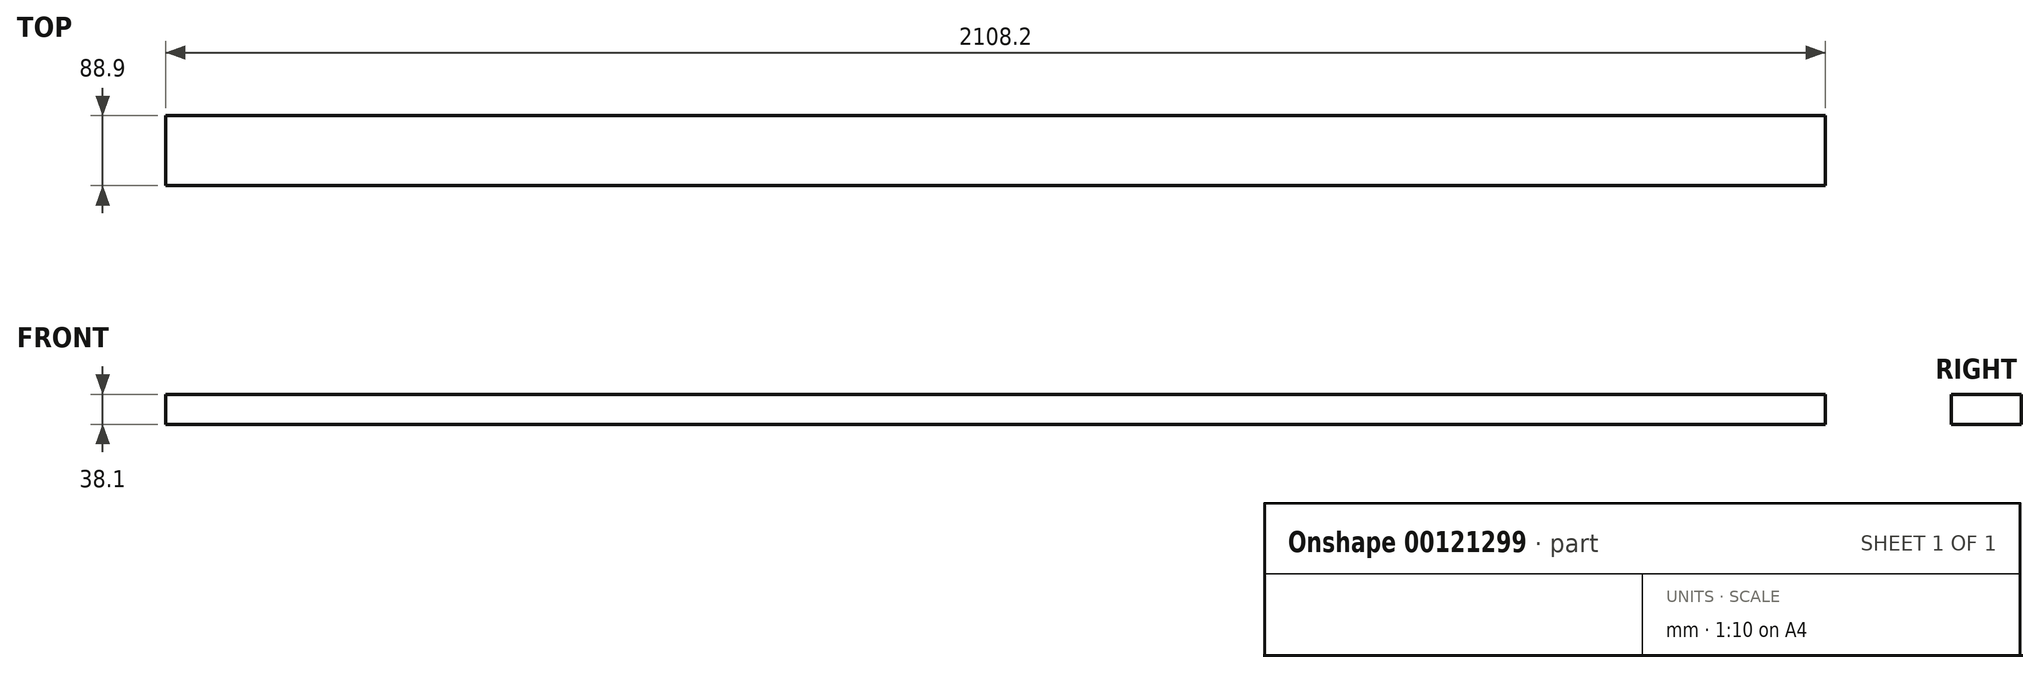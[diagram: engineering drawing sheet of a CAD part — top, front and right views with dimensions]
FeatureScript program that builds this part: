
annotation { "Feature Type Name" : "Feature", "Feature Type Description" : "" }
export const myFeature = defineFeature(function(context is Context, id is Id, definition is map)
    precondition{}
    {
        {
            var Q0;
            Q0=qCreatedBy(makeId("Front.planeOp"),FACE);
            var sketch = newSketch(context, id + "F0", { "sketchPlane" : qUnion([Q0])});
            skLineSegment(sketch, "E0.bottom", {"start": v(0, 0) * mm, "end": v(2108.2, 0) * mm});
            skLineSegment(sketch, "E0.top", {"start": v(0, 38.1) * mm, "end": v(2108.2, 38.1) * mm});
            skLineSegment(sketch, "E0.left", {"start": v(0, 0) * mm, "end": v(0, 38.1) * mm});
            skLineSegment(sketch, "E0.right", {"start": v(2108.2, 0) * mm, "end": v(2108.2, 38.1) * mm});
            skSolve(sketch);
        }
        {
            var Q0;
            Q0=makeQuery(id+"F0.imprint","IMPRINT",FACE,{"disambiguationData":[TD([[makeQuery(id+"F0.imprint","IMPRINT",EDGE,{"derivedFrom":sQuery(id+"F0.wireOp",EDGE,"E0.bottom")}),1.0]])]});
            extrude(context, id + "F1", {"entities" : qUnion([Q0]), "depth" : 88.9 * mm});
        }
    });
